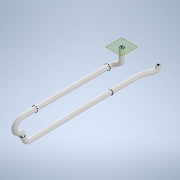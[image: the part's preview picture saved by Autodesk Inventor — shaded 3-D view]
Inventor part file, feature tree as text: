
AUTODESK INVENTOR PART (.ipt)
format: ipt  version: 2022 (Build 260153000, 153)  size: 242,176 bytes
history: native  units: mm
features: sketch x3, plane x1, sweep x1
ambient origin geometry x8: Origin, YZ Plane, XZ Plane, XY Plane, X Axis, Y Axis, Z Axis, Center Point
bodies: Solid1 (feature_tree)
feature tree (5):
  sketch  "3D Sketch1"
  sketch  "3D Sketch2"
  plane  "Work Plane1"
  sweep  "Sweep1"
  sketch  "Sketch1"  dims[d1=0.0mm d2=0.0mm d3=5.0mm d4=5.0mm d12=5.0mm d13=5.0mm d14=5.0mm d15=20.0mm d16=20.0mm d17=15.0mm d18=10.0mm d20=0.5mm]
